# Revit family: Camera-Security-Panasonic-Anti-severe-weather-PTZ-Network-SUD638X
name_source: partatom
category: Security Devices
revit_build: Autodesk Revit 2013 (Build: 20130531_2115(x64)
units: mm (PartAtom-declared; Revit-internal decimal feet)

## types (1)
- WV-SUD638
    Alarm Input Or Output Specification = ALARM IN 1(DAY/NIGHT IN, Auto time adjustment),ALARM IN 2(ALARM OUT), ALARM IN 3(AUX OUT),Relay connection (x1 for each)
    Angle Of View = 64
    Audio In = Yes
    Audio Out = Yes
    Communication Ports = 10Base-T / 100Base-TX, RJ45 connector
    Cost = 0 $
    Date Last Modified = October, 31, 2016
    Day Or Night = Yes
    Default Elevation = 48 "
    Description = Security Camera, Anti-severe Weather PTZ Network, WV-SUD638
    Equipment Abbreviation = SC
    Family Version = 1.0.0
    HFOV Max 169 = 64.00°
    HFOV Max 43 = 50.00°
    HFOV Min 169 = 2.30°
    HFOV Min 43 = 1.80°
    Has POE = Yes
    Horizontal Resolution 169 = 1920
    Horizontal Resolution 43 = 1280
    IP Or Analog = IP
    Indoor Or Outdoor = Outdoor
    Manufacturer = Panasonic
    Minimum Illumination = 0 lx
    Model = WV-SUD638
    Model Disclaimer = Contact Panasonic for more information
    Mounting Positions = Mount Dependent or Surface Mount
    Operational Humidity = 10% to 100%
    Operational Temperature = -58°F - 140°F
    Pan Max = 180.00°
    Pan Min = -180.00°
    Panning Range = 360° endless
    Part Description = Security Camera, Anti-severe Weather PTZ Network, WV-SUD638
    Part Number = WV-SUD638
    Power Active = 61.0 W
    Product Documentation Link = http://ssbu-t.psn-web.net
    Product Material = Paint - Panasonic - Silver
    Product Page URL = http://security.panasonic.com
    Provide Feedback = https://www.surveymonkey.com
    Regulatory Compliance = UL UL60950-1, C-UL CAN/CSA C22.2 No.60950-1, CE, IEC60950-1 FCC Part15 ClassA, ICES003 ClassA, EN55022 ClassB, EN55024
    Shock resistance = Compliant with IK10 (IEC 62262)
    Storage Temperature = -22°F - 158°F
    URL = http://security.panasonic.com
    VFOV Max 169 = 38.00°
    VFOV Max 43 = 38.00°
    VFOV Min 169 = 1.30°
    VFOV Min 43 = 1.30°
    Vandal Resistant = Yes
    Voltage AC = 100 V
    Voltage AC Max = 240 V
    Voltage AC Min = 100 V
    Water and Dust Resistance = Main body : IP66, IP67, IEC60529 measuring standard compatible, Type 4X(UL50), NEMA 4X compliant Waterproof RJ45 connector, Waterproof power connector,Waterproof I/O connector
    Weight = 18.70 lb
    Wide Dynamic Range = Yes
    z Const Pan Handle Length = 19.488 "
    z Const Tilt Base Length = 9.843 "
    z Const Tilt Base2 Length = 19.685 "
    z Const Tilt Handle Length = 11.811 "
    z Const Zero = 0 "
    z VV Viewpoint Depth Max = 2.61 "
    z VV Viewpoint Depth Min = 2.61 "

## geometry (parser evidence)
native form markers: Blend x8, Sweep x6
no freeform markers — native parametric forms only
